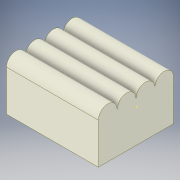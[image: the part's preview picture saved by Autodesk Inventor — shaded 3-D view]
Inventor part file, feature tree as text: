
AUTODESK INVENTOR PART (.ipt)
format: ipt  version: 2018 (Build 220112000, 112)  size: 121,856 bytes
history: native  units: in
note: dims shown in document units (in); Inventor stores cm internally (conversion verified against a paired STEP export)
features: sketch x4, extrude x2
ambient origin geometry x8: Origin, YZ Plane, XZ Plane, XY Plane, X Axis, Y Axis, Z Axis, Center Point
bodies: Solid1 (feature_tree)
feature tree (6):
  sketch  "Sketch1"  dims[d0=1.7717in d1=1.1811in]
  extrude  "Extrusion1"  Depth=1.7717in
  sketch  "Sketch3"  dims[d5=0.4429in]
  extrude  "Extrusion2"  Depth=2.1654in
  sketch  "Sketch2"  dims[d2=2.1654in d3=0.0in d4=0.4429in]
  sketch  "Sketch4"  dims[d6=0.4429in d7=0.4429in d8=2.3622in d9=0.0in]
